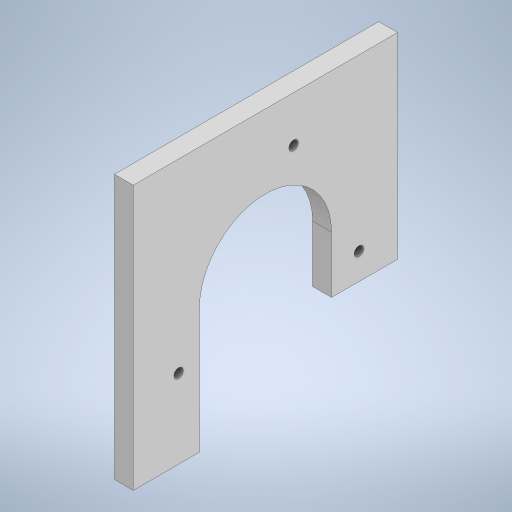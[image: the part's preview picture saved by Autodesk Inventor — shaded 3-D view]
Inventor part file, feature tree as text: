
AUTODESK INVENTOR PART (.ipt)
format: ipt  version: 2023 (Build 270158000, 158)  size: 302,592 bytes
history: native  units: mm
features: other x3, extrude x1, sketch x1, projected_geometry x1
ambient origin geometry x8: Origin, YZ Plane, XZ Plane, XY Plane, X Axis, Y Axis, Z Axis, Center Point
bodies: Body1 (feature_tree)
feature tree (6):
  other  "Твердое тело1"
  other  "РабПлоскость8"
  extrude  "Выдавливание5"  Depth=66.0mm
  other  "РабПлоскость7"
  sketch  "Эскиз6"
  projected_geometry  "Спроецированная петля1"
